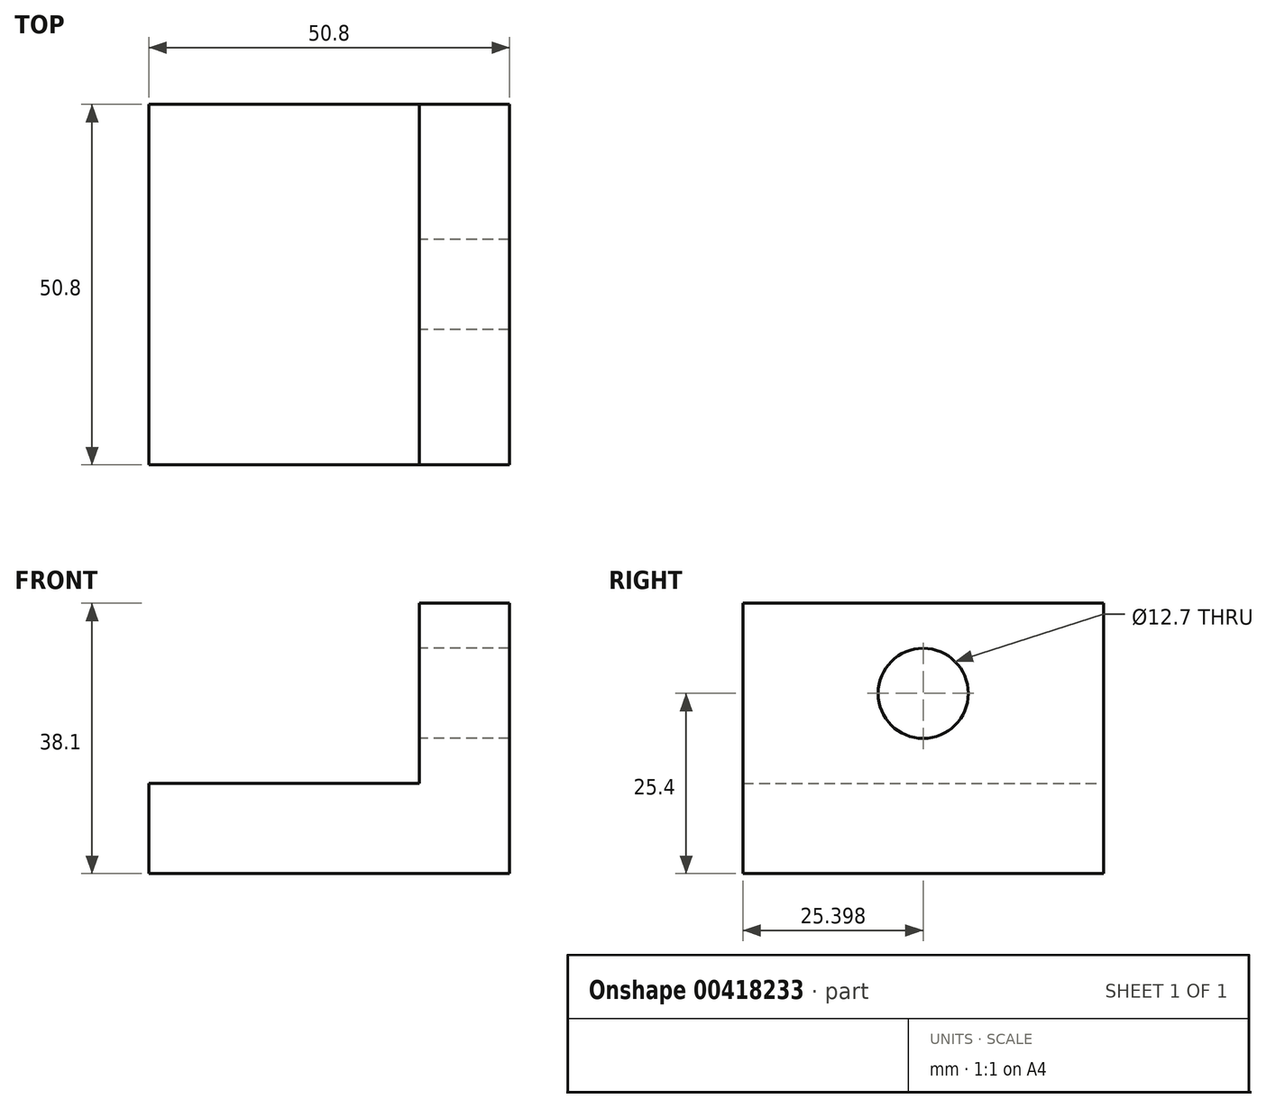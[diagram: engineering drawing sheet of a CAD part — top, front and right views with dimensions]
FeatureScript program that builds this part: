
annotation { "Feature Type Name" : "Feature", "Feature Type Description" : "" }
export const myFeature = defineFeature(function(context is Context, id is Id, definition is map)
    precondition{}
    {
        {
            var Q0;
            Q0=qCreatedBy(makeId("Top.planeOp"),FACE);
            var sketch = newSketch(context, id + "F0", { "sketchPlane" : qUnion([Q0])});
            skLineSegment(sketch, "E0.bottom", {"start": v(-60.76, -37.71) * mm, "end": v(-9.96, -37.71) * mm});
            skLineSegment(sketch, "E0.top", {"start": v(-60.76, 13.09) * mm, "end": v(-9.96, 13.09) * mm});
            skLineSegment(sketch, "E0.left", {"start": v(-60.76, -37.71) * mm, "end": v(-60.76, 13.09) * mm});
            skLineSegment(sketch, "E0.right", {"start": v(-9.96, -37.71) * mm, "end": v(-9.96, 13.09) * mm});
            skSolve(sketch);
        }
        {
            var Q0;
            Q0 = qSketchRegion(id + "F0", true);
            extrude(context, id + "F1", {"entities" : qUnion([Q0]), "depth" : 12.7 * mm});
        }
        {
            var Q0;
            Q0=makeQuery(id+"F1.opExtrude","CAP_FACE",FACE,{"disambiguationData":[OSD([sQuery(id+"F0.wireOp",EDGE,"E0.bottom"),sQuery(id+"F0.wireOp",EDGE,"E0.top"),sQuery(id+"F0.wireOp",EDGE,"E0.left"),sQuery(id+"F0.wireOp",EDGE,"E0.right")])],"isStart":false});
            var sketch = newSketch(context, id + "F2", { "sketchPlane" : qUnion([Q0])});
            skLineSegment(sketch, "E1", {"start": v(-9.96, -37.71) * mm, "end": v(-22.66, -37.71) * mm});
            skLineSegment(sketch, "E2", {"start": v(-22.66, 13.09) * mm, "end": v(-22.66, -37.71) * mm});
            skSolve(sketch);
        }
        {
            var Q0;
            Q0 = qSketchRegion(id + "F2", true);
            var Q1;
            Q1=makeQuery(id+"F2.imprint","IMPRINT",FACE,{"disambiguationData":[TD([[makeQuery(id+"F2.imprint","IMPRINT",EDGE,{"derivedFrom":sQuery(id+"F2.wireOp",EDGE,"E1")}),1.0]])]});
            extrude(context, id + "F3", {"entities" : qUnion([Q0, Q1]), "operationType" : NewBodyOperationType.ADD, "depth" : 25.4 * mm});
        }
        {
            var Q0;
            Q0=makeQuery(id+"F3.opExtrude","SWEPT_FACE",FACE,{"disambiguationData":[OSD([sQuery(id+"F2.wireOp",EDGE,"E2")])]});
            var sketch = newSketch(context, id + "F4", { "sketchPlane" : qUnion([Q0])});
            skCircle(sketch, "E3", {"center": v(12.31, 25.4) * mm, "radius": 6.35 * mm});
            skPoint(sketch, "E3.centerSnap0", {"position": v(12.31, 38.1) * mm});
            skPoint(sketch, "E3.centerSnap1", {"position": v(37.71, 25.4) * mm});
            skSolve(sketch);
        }
        {
            var Q0;
            Q0 = qSketchRegion(id + "F4", true);
            extrude(context, id + "F5", {"entities" : qUnion([Q0]), "operationType" : NewBodyOperationType.REMOVE, "endBound" : BoundingType.THROUGH_ALL, "oppositeDirection" : true, "depth" : 25.4 * mm});
        }
    });
